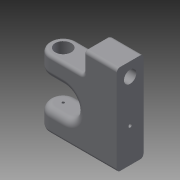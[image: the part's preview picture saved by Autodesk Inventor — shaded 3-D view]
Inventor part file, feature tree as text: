
AUTODESK INVENTOR PART (.ipt)
format: ipt  version: 2015 (Build 190159000, 159)  size: 214,528 bytes
history: native  units: mm
features: sketch x8, extrude x4, hole x3, revolve x1, mirror x1, fillet x1, projected_geometry x1
ambient origin geometry x8: Origin, YZ Plane, XZ Plane, XY Plane, X Axis, Y Axis, Z Axis, Center Point
bodies: Solid1 (feature_tree)
feature tree (19):
  extrude  "Extrusion1"  Depth=8.0mm
  extrude  "Extrusion2"  Depth=8.0mm
  extrude  "Extrusion3"  Depth=8.0mm TaperAngle=0.0deg
  revolve  "Revolution1"  [1 undecoded]
  mirror  "Mirror1"
  hole  "Hole1"  [1 undecoded]
  hole  "Hole2"  [1 undecoded]
  extrude  "Extrusion6"  Depth=4.0mm
  hole  "Hole3"  [1 undecoded]
  fillet  "Fillet1"  Radius=12.7mm
  sketch  "Sketch1"  dims[d0=20.0mm d1=8.0mm]
  sketch  "Sketch2"  dims[d2=20.4mm d3=0.0mm d4=8.0mm]
  sketch  "Sketch3"  dims[d5=8.0mm d6=19.6mm d7=0.0mm]
  sketch  "Sketch4"  dims[d8=4.8mm d9=4.1mm d10=0.0mm]
  sketch  "Sketch5"  dims[d11=1.7mm d12=90.0deg]
  sketch  "Sketch6"  dims[d13=0.75mm d14=6.0mm d15=4.0mm d16=2.0mm d17=90.0deg d18=8.0mm d19=20.594885mm]
  sketch  "Sketch9"  dims[d20=1.0mm d21=6.0mm d22=4.0mm d23=2.0mm d24=90.0deg d25=8.0mm d26=20.594885mm d34=8.0mm]
  sketch  "Sketch10"  dims[d35=12.7mm d36=4.0mm d37=10.0mm d38=0.0mm d39=12.7mm d40=3.7mm d41=6.0mm d42=4.0mm d43=2.0mm d44=90.0deg d45=8.0mm d46=20.594885mm d47=1.0mm d48=2.0mm]
  projected_geometry  "Project Cut Edges1"
note: 4 required parameter values undecoded (feature->parameter linkage not recoverable at this tier; creation-order binding heuristic only, values carry confidence <= 0.55)